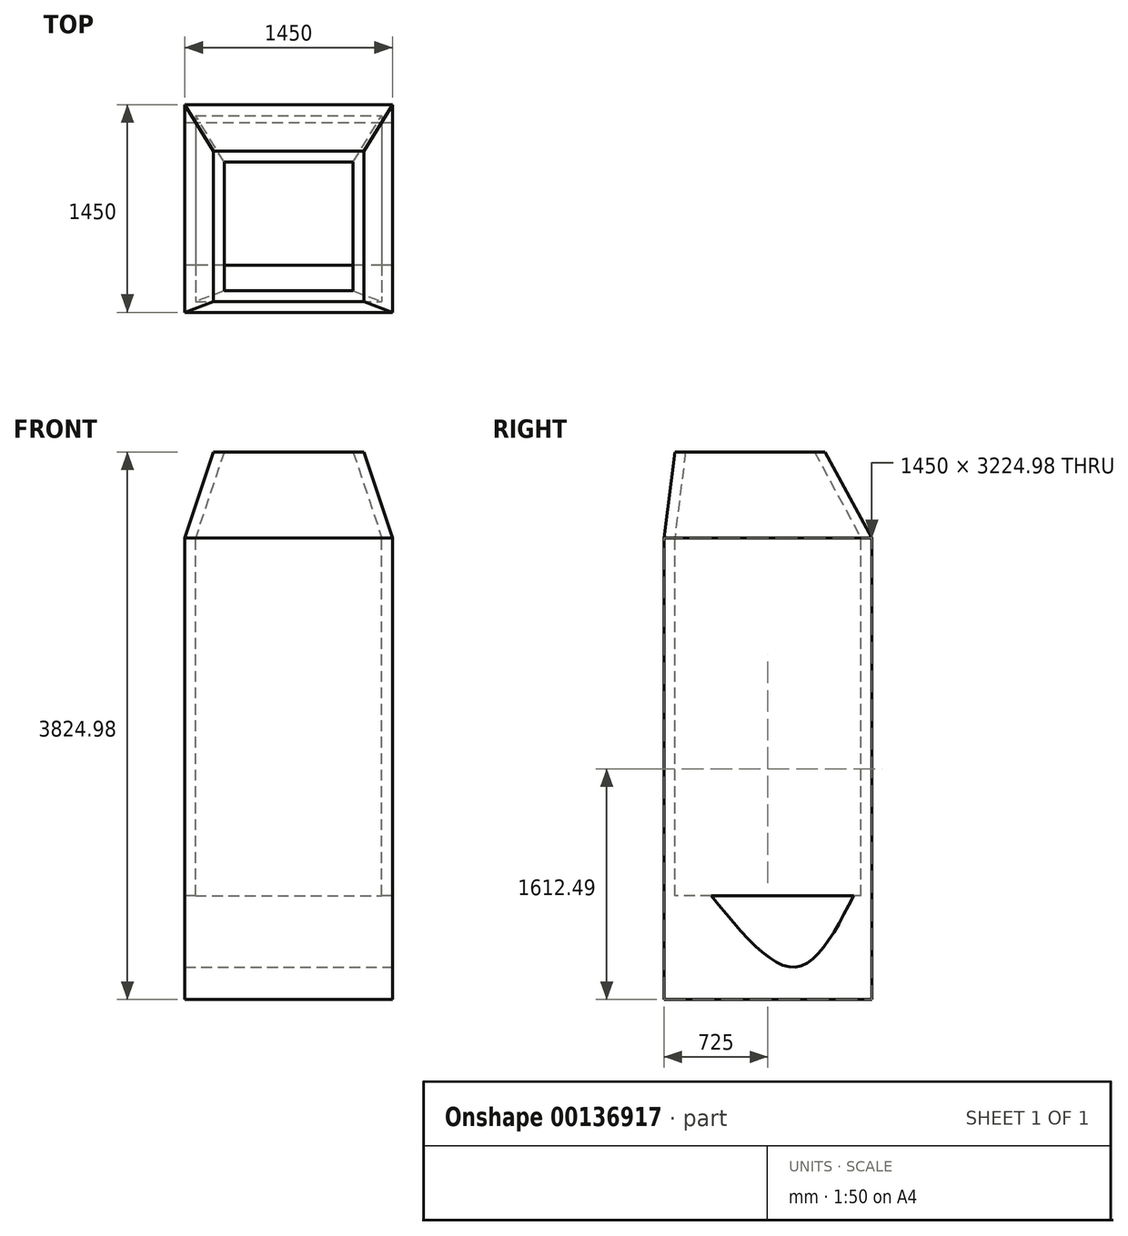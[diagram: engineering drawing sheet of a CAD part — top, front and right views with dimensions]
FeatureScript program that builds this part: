
annotation { "Feature Type Name" : "Feature", "Feature Type Description" : "" }
export const myFeature = defineFeature(function(context is Context, id is Id, definition is map)
    precondition{}
    {
        {
            var Q0;
            Q0=qCreatedBy(makeId("Top.planeOp"),FACE);
            var sketch = newSketch(context, id + "F0", { "sketchPlane" : qUnion([Q0])});
            skLineSegment(sketch, "E0.bottom", {"start": v(-525, -525) * mm, "end": v(525, -525) * mm});
            skLineSegment(sketch, "E0.top", {"start": v(-525, 525) * mm, "end": v(525, 525) * mm});
            skLineSegment(sketch, "E0.left", {"start": v(-525, -525) * mm, "end": v(-525, 525) * mm});
            skLineSegment(sketch, "E0.right", {"start": v(525, -525) * mm, "end": v(525, 525) * mm});
            skPoint(sketch, "E0.middle", {"position": v(0, 0) * mm});
            skSolve(sketch);
        }
        {
            var Q0;
            Q0=makeQuery(id+"F0.imprint","IMPRINT",FACE,{"disambiguationData":[TD([[makeQuery(id+"F0.imprint","IMPRINT",EDGE,{"derivedFrom":sQuery(id+"F0.wireOp",EDGE,"E0.bottom")}),1.0]])]});
            cPlane(context, id + "F1", {"entities" : qUnion([Q0]), "cplaneType" : CPlaneType.OFFSET, "offset" : 600 * mm, "oppositeDirection" : true, "width" : 150 * mm, "height" : 150 * mm});
        }
        {
            var Q0;
            Q0=qCreatedBy(id+"F1.planeOp",FACE);
            var sketch = newSketch(context, id + "F2", { "sketchPlane" : qUnion([Q0])});
            skLineSegment(sketch, "E1.bottom", {"start": v(-725, 850) * mm, "end": v(725, 850) * mm});
            skLineSegment(sketch, "E1.top", {"start": v(-725, -600) * mm, "end": v(725, -600) * mm});
            skLineSegment(sketch, "E1.left", {"start": v(-725, 850) * mm, "end": v(-725, -600) * mm});
            skLineSegment(sketch, "E1.right", {"start": v(725, 850) * mm, "end": v(725, -600) * mm});
            skSolve(sketch);
        }
        {
            var Q0;
            Q0=makeQuery(id+"F0.imprint","IMPRINT",FACE,{"disambiguationData":[TD([[makeQuery(id+"F0.imprint","IMPRINT",EDGE,{"derivedFrom":sQuery(id+"F0.wireOp",EDGE,"E0.bottom")}),1.0]])]});
            var Q1;
            Q1=makeQuery(id+"F2.imprint","IMPRINT",FACE,{"disambiguationData":[TD([[makeQuery(id+"F2.imprint","IMPRINT",EDGE,{"derivedFrom":sQuery(id+"F2.wireOp",EDGE,"E1.bottom")}),-1.0]])]});
            loft(context, id + "F3", {"sheetProfilesArray" : [{ "sheetProfileEntities" : qUnion([Q0]) }, { "sheetProfileEntities" : qUnion([Q1]) }]});
        }
        {
            var Q0;
            Q0=makeQuery(id+"F3.opLoft","CAP_FACE",FACE,{"disambiguationData":[OSD([makeQuery(id+"F0.imprint","IMPRINT",FACE,{"disambiguationData":[TD([[makeQuery(id+"F0.imprint","IMPRINT",EDGE,{"derivedFrom":sQuery(id+"F0.wireOp",EDGE,"E0.bottom")}),1.0]])]})])],"isStart":true});
            var sketch = newSketch(context, id + "F4", { "sketchPlane" : qUnion([Q0])});
            skLineSegment(sketch, "E2.bottom", {"start": v(-450, -450) * mm, "end": v(450, -450) * mm});
            skLineSegment(sketch, "E2.top", {"start": v(-450, 450) * mm, "end": v(450, 450) * mm});
            skLineSegment(sketch, "E2.left", {"start": v(-450, -450) * mm, "end": v(-450, 450) * mm});
            skLineSegment(sketch, "E2.right", {"start": v(450, -450) * mm, "end": v(450, 450) * mm});
            skPoint(sketch, "E2.middle", {"position": v(0, 0) * mm});
            skSolve(sketch);
        }
        {
            var Q0;
            Q0=makeQuery(id+"F3.opLoft","CAP_FACE",FACE,{"disambiguationData":[OSD([makeQuery(id+"F2.imprint","IMPRINT",FACE,{"disambiguationData":[TD([[makeQuery(id+"F2.imprint","IMPRINT",EDGE,{"derivedFrom":sQuery(id+"F2.wireOp",EDGE,"E1.bottom")}),-1.0]])]})])],"isStart":true});
            var sketch = newSketch(context, id + "F5", { "sketchPlane" : qUnion([Q0])});
            skLineSegment(sketch, "E3.bottom", {"start": v(-650, -775) * mm, "end": v(650, -775) * mm});
            skLineSegment(sketch, "E3.top", {"start": v(-650, 525) * mm, "end": v(650, 525) * mm});
            skLineSegment(sketch, "E3.left", {"start": v(-650, -775) * mm, "end": v(-650, 525) * mm});
            skLineSegment(sketch, "E3.right", {"start": v(650, -775) * mm, "end": v(650, 525) * mm});
            skPoint(sketch, "E3.middle", {"position": v(0, -125) * mm});
            skSolve(sketch);
        }
        {
            var Q1;
            Q1=makeQuery(id+"F4.imprint","IMPRINT",FACE,{"disambiguationData":[TD([[makeQuery(id+"F4.imprint","IMPRINT",EDGE,{"derivedFrom":sQuery(id+"F4.wireOp",EDGE,"E2.bottom")}),1.0]])]});
            var Q2;
            Q2=makeQuery(id+"F5.imprint","IMPRINT",FACE,{"disambiguationData":[TD([[makeQuery(id+"F5.imprint","IMPRINT",EDGE,{"derivedFrom":sQuery(id+"F5.wireOp",EDGE,"E3.bottom")}),1.0]])]});
            loft(context, id + "F6", {"operationType" : NewBodyOperationType.REMOVE, "sheetProfilesArray" : [{ "sheetProfileEntities" : qUnion([Q1]) }, { "sheetProfileEntities" : qUnion([Q2]) }]});
        }
        {
            var Q0;
            Q0=makeQuery(id+"F3.opLoft","CAP_FACE",FACE,{"disambiguationData":[OSD([makeQuery(id+"F2.imprint","IMPRINT",FACE,{"disambiguationData":[TD([[makeQuery(id+"F2.imprint","IMPRINT",EDGE,{"derivedFrom":sQuery(id+"F2.wireOp",EDGE,"E1.bottom")}),-1.0]])]})])],"isStart":true});
            extrude(context, id + "F7", {"entities" : qUnion([Q0]), "operationType" : NewBodyOperationType.ADD, "depth" : 2500 * mm});
        }
        {
            var Q0;
            Q0=qCreatedBy(makeId("Right.planeOp"),FACE);
            var sketch = newSketch(context, id + "F8", { "sketchPlane" : qUnion([Q0])});
            skLineSegment(sketch, "E4", {"start": v(-600, -3100) * mm, "end": v(-600, -3824.98) * mm});
            skLineSegment(sketch, "E5", {"start": v(-600, -3824.98) * mm, "end": v(850, -3824.98) * mm});
            skLineSegment(sketch, "E6", {"start": v(850, -3824.98) * mm, "end": v(850, -3100) * mm});
            skLineSegment(sketch, "E7", {"start": v(-600, -3100) * mm, "end": v(-270.71, -3100) * mm});
            skFitSpline(sketch, "E8", {"points": [v(-270.71, -3100) * mm, v(318.85, -3598.1) * mm, v(723.32, -3100) * mm], "startDerivative": vector(1200.1, -1474.44) * mm, "endDerivative": vector(781.53, 1520.5) * mm});
            skLineSegment(sketch, "E9", {"start": v(723.32, -3100) * mm, "end": v(850, -3100) * mm});
            skSolve(sketch);
        }
        {
            var Q0;
            Q0=makeQuery(id+"F8.imprint","IMPRINT",FACE,{"disambiguationData":[TD([[makeQuery(id+"F8.imprint","IMPRINT",EDGE,{"derivedFrom":sQuery(id+"F8.wireOp",EDGE,"E4")}),1.0]])]});
            extrude(context, id + "F9", {"entities" : qUnion([Q0]), "operationType" : NewBodyOperationType.ADD, "endBound" : BoundingType.SYMMETRIC, "depth" : 1450 * mm});
        }
    });
